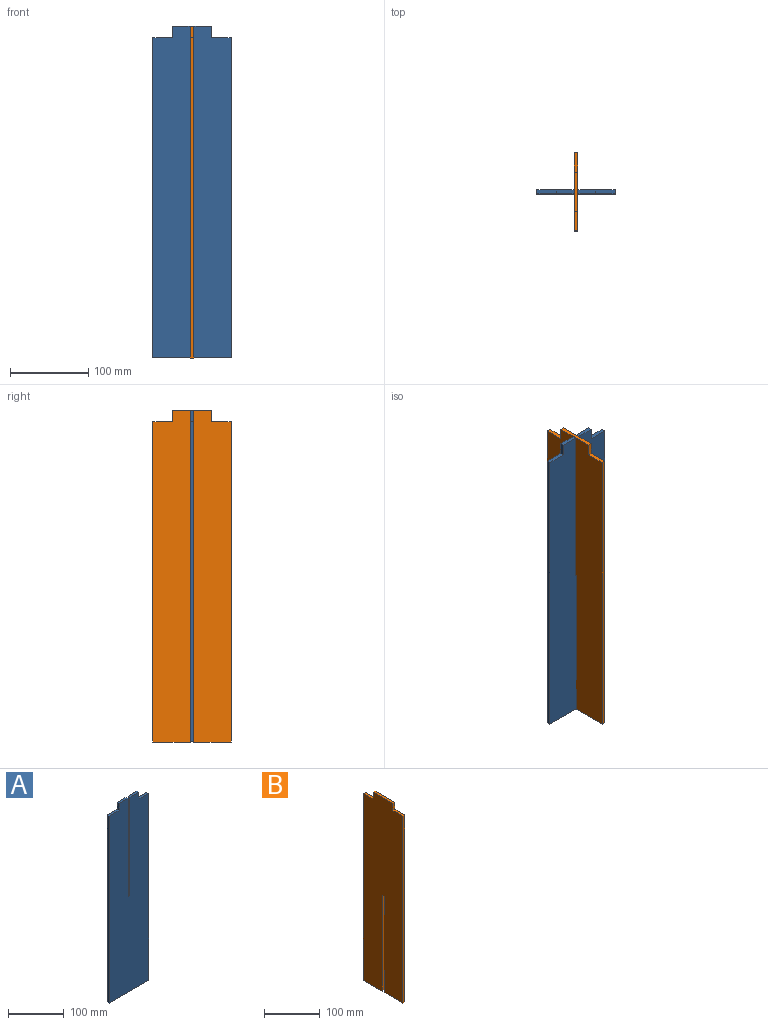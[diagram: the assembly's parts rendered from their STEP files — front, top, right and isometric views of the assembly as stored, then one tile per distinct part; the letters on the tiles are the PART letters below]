
ASSEMBLY  parts=2 mates=1
PART A: 14 faces, bbox 100x5x425 mm
  f0: plane 5x5mm, normal (0,0,1), area 25mm2, adj f1,f11,f12,f13
  f1: plane 215x5mm, normal (1,0,0), area 1075mm2, adj f0,f2,f12,f13
  f2: plane 22.5x5mm, normal (0,0,1), area 112.5mm2, adj f1,f3,f12,f13
  f3: plane 15x5mm, normal (-1,0,0), area 75mm2, adj f2,f4,f12,f13
  f4: plane 25x5mm, normal (0,0,1), area 125mm2, adj f3,f5,f12,f13
  f5: plane 410x5mm, normal (-1,0,0), area 2050mm2, adj f4,f6,f12,f13
  f6: plane 100x5mm, normal (0,0,-1), area 500mm2, adj f5,f7,f12,f13
  f7: plane 410x5mm, normal (1,0,0), area 2050mm2, adj f6,f8,f12,f13
  f8: plane 25x5mm, normal (0,0,1), area 125mm2, adj f7,f9,f12,f13
  f9: plane 15x5mm, normal (1,0,0), area 75mm2, adj f8,f10,f12,f13
  f10: plane 22.5x5mm, normal (0,0,1), area 112.5mm2, adj f9,f11,f12,f13
  f11: plane 215x5mm, normal (-1,0,0), area 1075mm2, adj f0,f10,f12,f13
  f12: plane 425x100mm, normal (0,-1,0), area 40675mm2, adj f0,f1,f2,f3,f4,f5,f6,f7
  f13: plane 425x100mm, normal (0,1,0), area 40675mm2, adj f0,f1,f2,f3,f4,f5,f6,f7
PART B: 14 faces, bbox 5x100x425 mm
  f0: plane 47.5x5mm, normal (0,0,-1), area 237.5mm2, adj f1,f11,f12,f13
  f1: plane 210x5mm, normal (0,1,0), area 1050mm2, adj f0,f2,f12,f13
  f2: plane 5x5mm, normal (0,0,-1), area 25mm2, adj f1,f3,f12,f13
  f3: plane 210x5mm, normal (0,-1,0), area 1050mm2, adj f2,f4,f12,f13
  f4: plane 47.5x5mm, normal (0,0,-1), area 237.5mm2, adj f3,f5,f12,f13
  f5: plane 410x5mm, normal (0,1,0), area 2050mm2, adj f4,f6,f12,f13
  f6: plane 25x5mm, normal (0,0,1), area 125mm2, adj f5,f7,f12,f13
  f7: plane 15x5mm, normal (0,1,0), area 75mm2, adj f6,f8,f12,f13
  f8: plane 50x5mm, normal (0,0,1), area 250mm2, adj f7,f9,f12,f13
  f9: plane 15x5mm, normal (0,-1,0), area 75mm2, adj f8,f10,f12,f13
  f10: plane 25x5mm, normal (0,0,1), area 125mm2, adj f9,f11,f12,f13
  f11: plane 410x5mm, normal (0,-1,0), area 2050mm2, adj f0,f10,f12,f13
  f12: plane 425x100mm, normal (1,0,0), area 40700mm2, adj f0,f1,f2,f3,f4,f5,f6,f7
  f13: plane 425x100mm, normal (-1,0,0), area 40700mm2, adj f0,f1,f2,f3,f4,f5,f6,f7
PLACE A t=(126.38,399.32,-3.98)mm
PLACE B t=(73.88,446.82,-3.98)mm
MATE fastened A.f0 <-> B.f2  axis (0,0,1) through (76.38,396.82,206.02)mm
